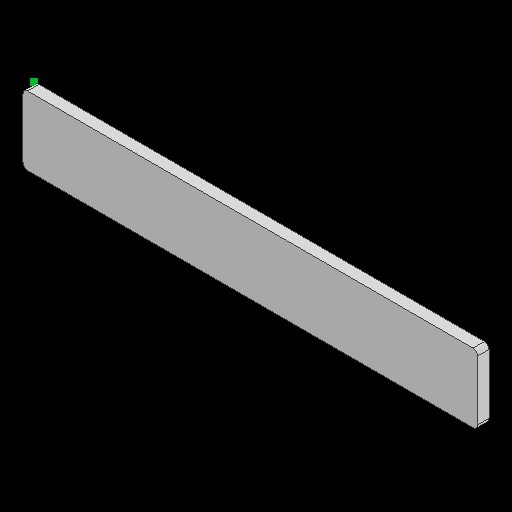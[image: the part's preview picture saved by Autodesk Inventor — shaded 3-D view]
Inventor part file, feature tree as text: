
AUTODESK INVENTOR PART (.ipt)
format: ipt  version: 2025.1 (Build 291241000, 241)  size: 158,720 bytes
history: native  units: in
note: dims shown in document units (in); Inventor stores cm internally (conversion verified against a paired STEP export)
features: sketch x3, other x2, extrude x2, fillet x1, projected_geometry x1
ambient origin geometry x8: Origin, YZ Plane, XZ Plane, XY Plane, X Axis, Y Axis, Z Axis, Center Point
bodies: Body1 (feature_tree)
feature tree (9):
  other  "솔리드1"
  sketch  "스케치1"
  extrude  "돌출1"  Depth=7.7953in
  extrude  "돌출2"  Depth=1.1811in
  fillet  "모깎기1"  Radius=0.0787in
  sketch  "스케치2"
  other  "스케치 - 직사각형 패턴1"
  sketch  "스케치3"
  projected_geometry  "투영된 루프1"
